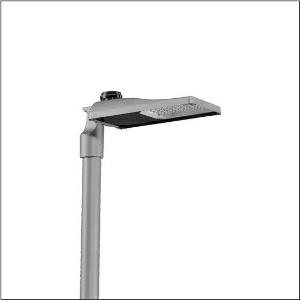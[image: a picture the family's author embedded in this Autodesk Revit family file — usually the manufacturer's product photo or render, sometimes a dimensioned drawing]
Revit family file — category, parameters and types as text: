
# Revit family: streetlight_sl_31_mini___st1_0a_5xh2d35n08ga_ac29
name_source: partatom
category: Lighting Fixtures
units: mm (PartAtom-declared; Revit-internal decimal feet)

## family parameters
Cut with Voids When Loaded = No
Host = Face
Light Source = No
Part Type = Normal
Room Calculation Point = No
Round Connector Dimension = Use Diameter
Shared = No

## types (1)
- --- (1 x LED, 5710 lm, 37.3 W, 3000K)
    Apparent Load = 37 VA
    CIE Flux Codes = 37 72 97 100 100
    Color Rendering = 70
    Color Temperature = 3000K
    Default Elevation = 1800 mm
    Description = Streetlight SL 31 mini NEMA (7pin), Desk-Remote mast luminaire for post-top, side-entry; light control with lens of PMMA; light distribution: ST1.0a, direct asymmetric distribution, for standard-compliant lighting for roads and squares; LED: luminous flux: 5.710lm, light colour: 730, colour temperature: 3000K; luminous efficacy: 153,1lm/W; control: pre-setting: linear dimming characteristic, flexible luminous flux parameterisation, time-dependent luminous flux control, constant luminous flux control, intelligent temperature release in ECG and LED module, overheat protection; luminaire housing, of diecast aluminium, SITECO metallic grey (DB 702S), corrosivity category C5 high according to DIN EN ISO 12944; cover of toughened safety glass, transparent, mast flange of diecast aluminium, SITECO metallic grey (DB 702S), spigot size: 76/60mm, mast flange included unmounted; cable length: 6,5m, connection cable pre-assembled; mains connection: 220..240V, AC, 50/60Hz; power consumption (at start of service life): 37,3W / (at end of service life): 38,7W / (with reduced operation 50%): 17,5W; protection rating (complete): IP66; insulation class (complete): insulation class I (protective earthing); impact resistance: IK10; certification: CE, ENEC, ENEC+, VDE, UKCA; permissible operating ambient temperature for outdoor applications: -40..+50°C; packaging unit: 1 piece

Light Distribution: ST1.0a
    Height = 76 mm
    Lamp = 1 x LED
    Lamp Light Flux = 5710 lm
    Lamp Power = 37.3 W
    Lamp count = 1
    Length = 547 mm
    Luminous efficacy = 153 lm/W
    Manufacturer = Siteco
    ModVariant = No
    Model = 5XH2D35N08GA
    Number of Poles = 1
    OnlyDefault = Yes
    Power Factor = 1
    Product Name = Streetlight SL 31 mini | ST1.0a
    Product group = mast luminaire | pylon top
    ProductGroupID = 6100
    Protection Class = Protection class I
    Protection Degree = IP 66
    RLX_Detail_Level = 1
    RLX_Emergency_Light_Flux = 0 lm
    RLX_Emergency_Type = 0
    RLX_Emergency_Type_DB = No
    RlxData = <blob elided: 40257 chars, md5=a0a420e8>
    Socket = socket
    Standby Power = 0 W
    System Light Flux = 5710 lm
    System Power = 37 W
    Type Comments = factory setting: luminous flux: 100 % | dim-lin: 254 | 386 mA
    Type Image = l_1300322.jpg
    URL = http://relux.com
    VarID = @adj_061333
    Voltage = 0 V
    Weight = 0.00 kg
    Width = 265 mm

## geometry (parser evidence)
native form markers: Blend x4, Sweep x9
no freeform markers — native parametric forms only
